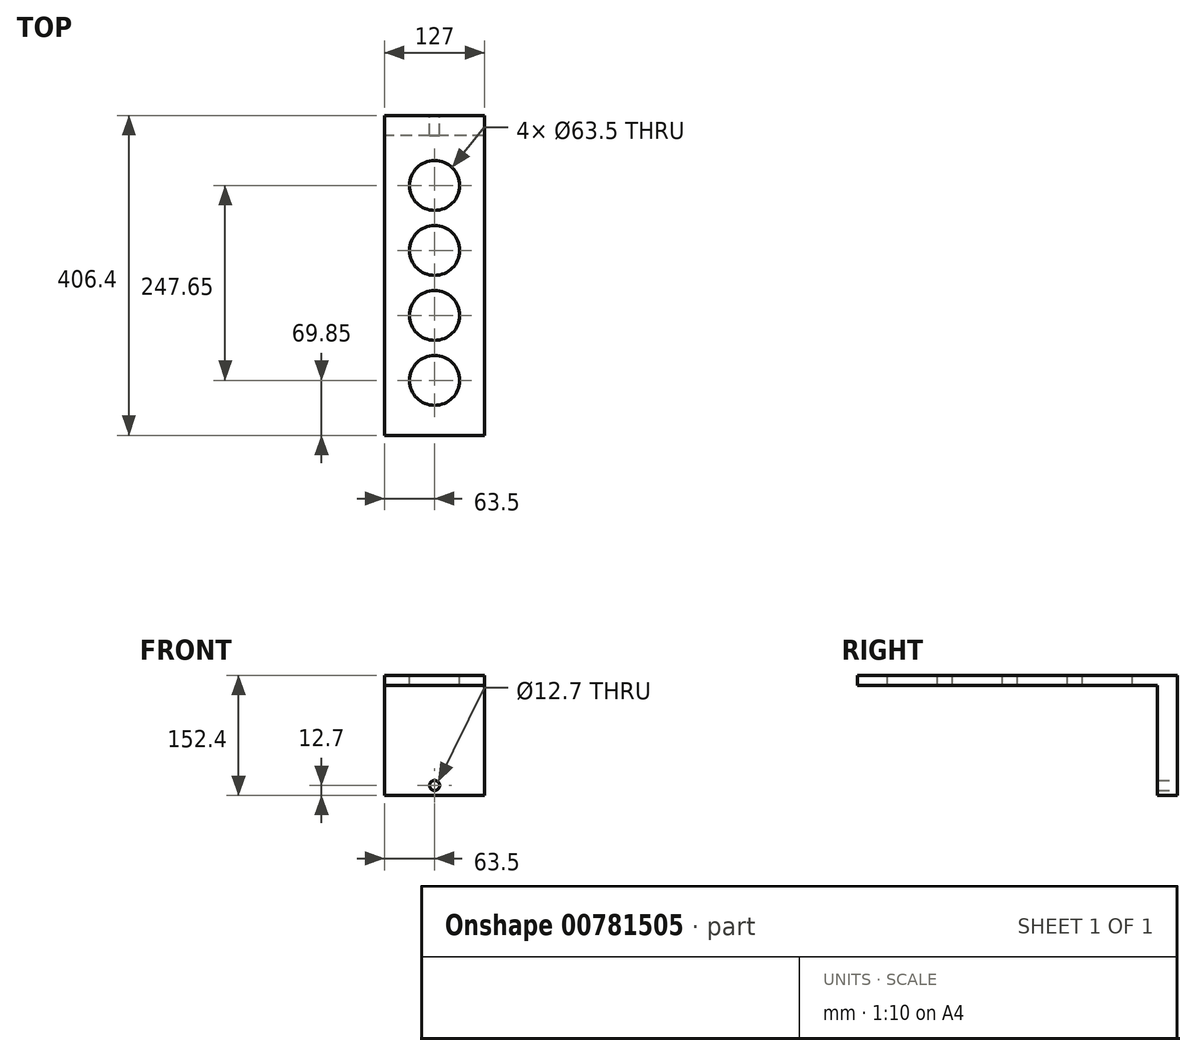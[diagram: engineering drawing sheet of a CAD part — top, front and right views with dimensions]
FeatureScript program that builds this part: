
annotation { "Feature Type Name" : "Feature", "Feature Type Description" : "" }
export const myFeature = defineFeature(function(context is Context, id is Id, definition is map)
    precondition{}
    {
        {
            var Q0;
            Q0=qCreatedBy(makeId("Front.planeOp"),FACE);
            var sketch = newSketch(context, id + "F0", { "sketchPlane" : qUnion([Q0])});
            skCircle(sketch, "E0", {"center": v(0, 0) * mm, "radius": 6.35 * mm});
            skLineSegment(sketch, "E1.bottom", {"start": v(63.5, -12.7) * mm, "end": v(-63.5, -12.7) * mm});
            skLineSegment(sketch, "E1.top", {"start": v(63.5, 139.7) * mm, "end": v(-63.5, 139.7) * mm});
            skLineSegment(sketch, "E1.left", {"start": v(63.5, -12.7) * mm, "end": v(63.5, 139.7) * mm});
            skLineSegment(sketch, "E1.right", {"start": v(-63.5, -12.7) * mm, "end": v(-63.5, 139.7) * mm});
            skLineSegment(sketch, "E2", {"start": v(-63.5, 0) * mm, "end": v(63.5, 0) * mm, "construction": true});
            skSolve(sketch);
        }
        {
            var Q0;
            Q0 = qSketchRegion(id + "F0", true);
            extrude(context, id + "F1", {"entities" : qUnion([Q0]), "depth" : 25.4 * mm, "offsetDistance" : 25.4 * mm});
        }
        {
            var Q0;
            Q0=makeQuery(id+"F1.opExtrude","CAP_FACE",FACE,{"disambiguationData":[OSD([sQuery(id+"F0.wireOp",EDGE,"E0"),sQuery(id+"F0.wireOp",EDGE,"E1.bottom"),sQuery(id+"F0.wireOp",EDGE,"E1.top"),sQuery(id+"F0.wireOp",EDGE,"E1.left"),sQuery(id+"F0.wireOp",EDGE,"E1.right")])],"isStart":false});
            var sketch = newSketch(context, id + "F2", { "sketchPlane" : qUnion([Q0])});
            skLineSegment(sketch, "E3.bottom", {"start": v(-63.5, 139.7) * mm, "end": v(63.5, 139.7) * mm});
            skLineSegment(sketch, "E3.top", {"start": v(-63.5, 127) * mm, "end": v(63.5, 127) * mm});
            skLineSegment(sketch, "E3.left", {"start": v(-63.5, 139.7) * mm, "end": v(-63.5, 127) * mm});
            skLineSegment(sketch, "E3.right", {"start": v(63.5, 139.7) * mm, "end": v(63.5, 127) * mm});
            skSolve(sketch);
        }
        {
            var Q0;
            Q0 = qSketchRegion(id + "F2", true);
            extrude(context, id + "F3", {"entities" : qUnion([Q0]), "operationType" : NewBodyOperationType.ADD, "depth" : 381 * mm, "offsetDistance" : 25.4 * mm});
        }
        {
            var Q0;
            Q0=makeQuery(id+"F3.boolean.opBoolean","MERGE",FACE,{"derivedFrom":[makeQuery(id+"F1.opExtrude","SWEPT_FACE",FACE,{"disambiguationData":[OSD([sQuery(id+"F0.wireOp",EDGE,"E1.top")])]}),makeQuery(id+"F3.opExtrude","SWEPT_FACE",FACE,{"disambiguationData":[OSD([sQuery(id+"F2.wireOp",EDGE,"E3.bottom")])]})]});
            var sketch = newSketch(context, id + "F4", { "sketchPlane" : qUnion([Q0])});
            skCircle(sketch, "E4", {"center": v(0, -88.9) * mm, "radius": 31.75 * mm});
            skCircle(sketch, "E5", {"center": v(0, -171.45) * mm, "radius": 31.75 * mm});
            skCircle(sketch, "E6", {"center": v(0, -254) * mm, "radius": 31.75 * mm});
            skCircle(sketch, "E7", {"center": v(0, -336.55) * mm, "radius": 31.75 * mm});
            skLineSegment(sketch, "E8", {"start": v(0, -88.9) * mm, "end": v(0, -171.45) * mm, "construction": true});
            skLineSegment(sketch, "E9", {"start": v(0, -254) * mm, "end": v(0, -171.45) * mm, "construction": true});
            skLineSegment(sketch, "E10", {"start": v(0, -254) * mm, "end": v(0, -336.55) * mm, "construction": true});
            skSolve(sketch);
        }
        {
            var Q0;
            Q0 = qSketchRegion(id + "F4", true);
            extrude(context, id + "F5", {"entities" : qUnion([Q0]), "operationType" : NewBodyOperationType.REMOVE, "oppositeDirection" : true, "depth" : 25.4 * mm, "offsetDistance" : 25.4 * mm});
        }
    });
